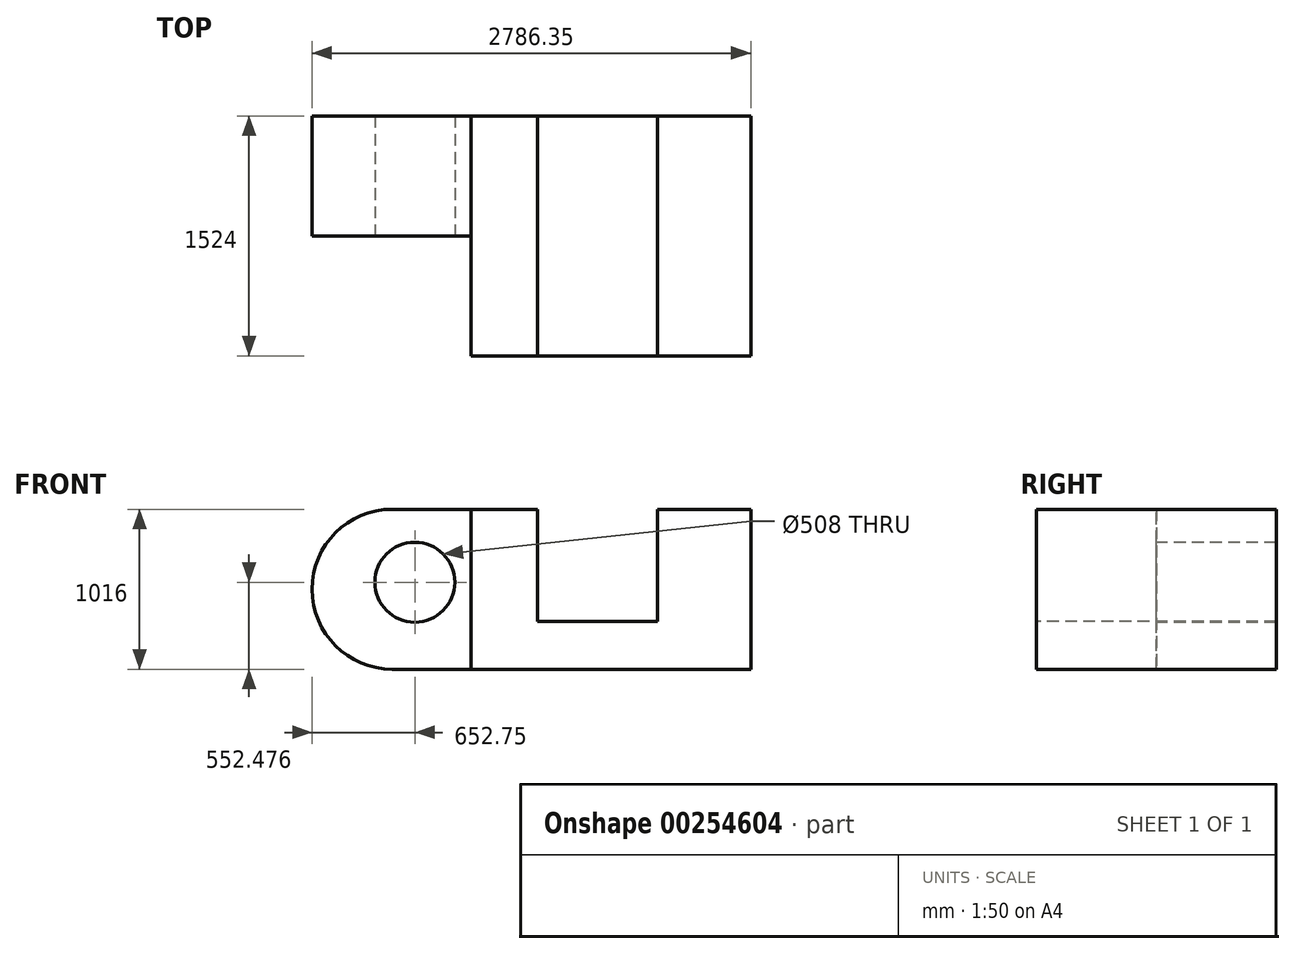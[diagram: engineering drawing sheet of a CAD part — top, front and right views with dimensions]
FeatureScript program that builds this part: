
annotation { "Feature Type Name" : "Feature", "Feature Type Description" : "" }
export const myFeature = defineFeature(function(context is Context, id is Id, definition is map)
    precondition{}
    {
        {
            var Q0;
            Q0=qCreatedBy(makeId("Front.planeOp"),FACE);
            var sketch = newSketch(context, id + "F0", { "sketchPlane" : qUnion([Q0])});
            skLineSegment(sketch, "E0.bottom", {"start": v(-889.52, 576.44) * mm, "end": v(888.48, 576.44) * mm});
            skLineSegment(sketch, "E0.top", {"start": v(-889.52, -439.56) * mm, "end": v(888.48, -439.56) * mm});
            skLineSegment(sketch, "E0.left", {"start": v(-889.52, 576.44) * mm, "end": v(-889.52, -439.56) * mm});
            skLineSegment(sketch, "E0.right", {"start": v(888.48, 576.44) * mm, "end": v(888.48, -439.56) * mm});
            skSolve(sketch);
        }
        {
            var Q0;
            Q0 = qSketchRegion(id + "F0", true);
            extrude(context, id + "F1", {"entities" : qUnion([Q0]), "depth" : 1524 * mm});
        }
        {
            var Q0;
            Q0=makeQuery(id+"F1.opExtrude","CAP_FACE",FACE,{"disambiguationData":[OSD([sQuery(id+"F0.wireOp",EDGE,"E0.bottom"),sQuery(id+"F0.wireOp",EDGE,"E0.top"),sQuery(id+"F0.wireOp",EDGE,"E0.left"),sQuery(id+"F0.wireOp",EDGE,"E0.right")])],"isStart":false});
            var sketch = newSketch(context, id + "F2", { "sketchPlane" : qUnion([Q0])});
            skLineSegment(sketch, "E1.bottom", {"start": v(-467.3, 576.44) * mm, "end": v(294.7, 576.44) * mm});
            skLineSegment(sketch, "E1.top", {"start": v(-467.3, -134.76) * mm, "end": v(294.7, -134.76) * mm});
            skLineSegment(sketch, "E1.left", {"start": v(-467.3, 576.44) * mm, "end": v(-467.3, -134.76) * mm});
            skLineSegment(sketch, "E1.right", {"start": v(294.7, 576.44) * mm, "end": v(294.7, -134.76) * mm});
            skSolve(sketch);
        }
        {
            var Q0;
            Q0 = qSketchRegion(id + "F2", true);
            extrude(context, id + "F3", {"entities" : qUnion([Q0]), "operationType" : NewBodyOperationType.REMOVE, "oppositeDirection" : true, "depth" : 1524 * mm});
        }
        {
            var Q0;
            Q0=makeQuery(id+"F1.opExtrude","CAP_FACE",FACE,{"disambiguationData":[OSD([sQuery(id+"F0.wireOp",EDGE,"E0.bottom"),sQuery(id+"F0.wireOp",EDGE,"E0.top"),sQuery(id+"F0.wireOp",EDGE,"E0.left"),sQuery(id+"F0.wireOp",EDGE,"E0.right")])],"isStart":true});
            var sketch = newSketch(context, id + "F4", { "sketchPlane" : qUnion([Q0])});
            skLineSegment(sketch, "E2", {"start": v(889.52, 576.44) * mm, "end": v(1389.87, 576.44) * mm});
            skLineSegment(sketch, "E3", {"start": v(889.52, -439.56) * mm, "end": v(1389.87, -439.56) * mm});
            skArc(sketch, "E4", {"start": v(1389.87, -439.56) * mm, "mid": v(1897.87, 68.44) * mm, "end": v(1389.87, 576.44) * mm});
            skSolve(sketch);
        }
        {
            var Q0;
            Q0 = qSketchRegion(id + "F4", true);
            var Q1;
            Q1=makeQuery(id+"F4.imprint","IMPRINT",FACE,{"disambiguationData":[TD([[makeQuery(id+"F4.imprint","IMPRINT",EDGE,{"derivedFrom":sQuery(id+"F4.wireOp",EDGE,"E2")}),-1.0]])]});
            extrude(context, id + "F5", {"entities" : qUnion([Q0, Q1]), "oppositeDirection" : true, "depth" : 762 * mm});
        }
        {
            var Q0;
            Q0=makeQuery(id+"F5.opExtrude","CAP_FACE",FACE,{"disambiguationData":[OSD([sQuery(id+"F0.wireOp",EDGE,"E0.left"),sQuery(id+"F4.wireOp",EDGE,"E2"),sQuery(id+"F4.wireOp",EDGE,"E3"),sQuery(id+"F4.wireOp",EDGE,"E4")])],"isStart":false});
            var sketch = newSketch(context, id + "F6", { "sketchPlane" : qUnion([Q0])});
            skCircle(sketch, "E5", {"center": v(-1245.12, 112.92) * mm, "radius": 254 * mm});
            skSolve(sketch);
        }
        {
            var Q0;
            Q0 = qSketchRegion(id + "F6", true);
            extrude(context, id + "F7", {"entities" : qUnion([Q0]), "operationType" : NewBodyOperationType.REMOVE, "oppositeDirection" : true, "depth" : 762 * mm});
        }
    });
